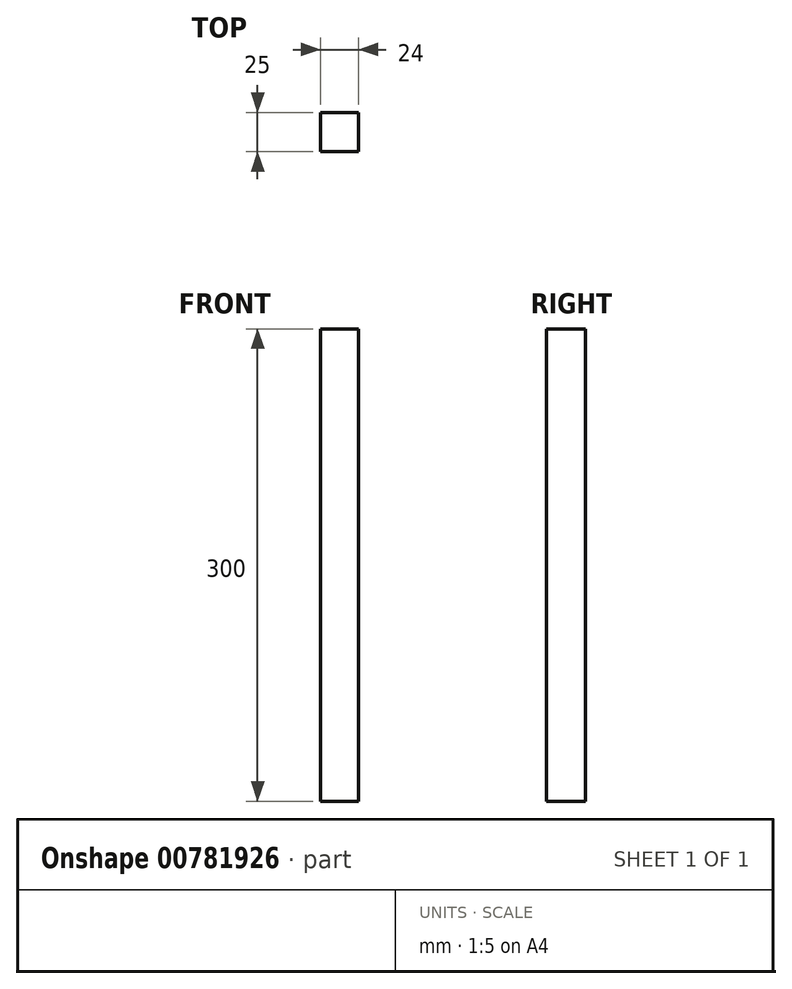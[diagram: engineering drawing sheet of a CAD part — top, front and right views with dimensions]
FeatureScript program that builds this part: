
annotation { "Feature Type Name" : "Feature", "Feature Type Description" : "" }
export const myFeature = defineFeature(function(context is Context, id is Id, definition is map)
    precondition{}
    {
        {
            var Q0;
            Q0=qCreatedBy(makeId("Front.planeOp"),FACE);
            var sketch = newSketch(context, id + "F0", { "sketchPlane" : qUnion([Q0])});
            skLineSegment(sketch, "E0.bottom", {"start": v(11.71, 287.54) * mm, "end": v(-288.29, 287.54) * mm});
            skLineSegment(sketch, "E0.top", {"start": v(11.71, -12.46) * mm, "end": v(-288.29, -12.46) * mm});
            skLineSegment(sketch, "E0.left", {"start": v(11.71, 287.54) * mm, "end": v(11.71, -12.46) * mm});
            skLineSegment(sketch, "E0.right", {"start": v(-12.29, 287.54) * mm, "end": v(-12.29, -12.46) * mm});
            skSolve(sketch);
        }
        {
            var Q0;
            Q0=qSketchRegion(id+"F0",true);
            extrude(context, id + "F1", {"entities" : qUnion([Q0]), "endBound" : BoundingType.SYMMETRIC, "depth" : 25 * mm, "offsetDistance" : 25 * mm});
        }
    });
